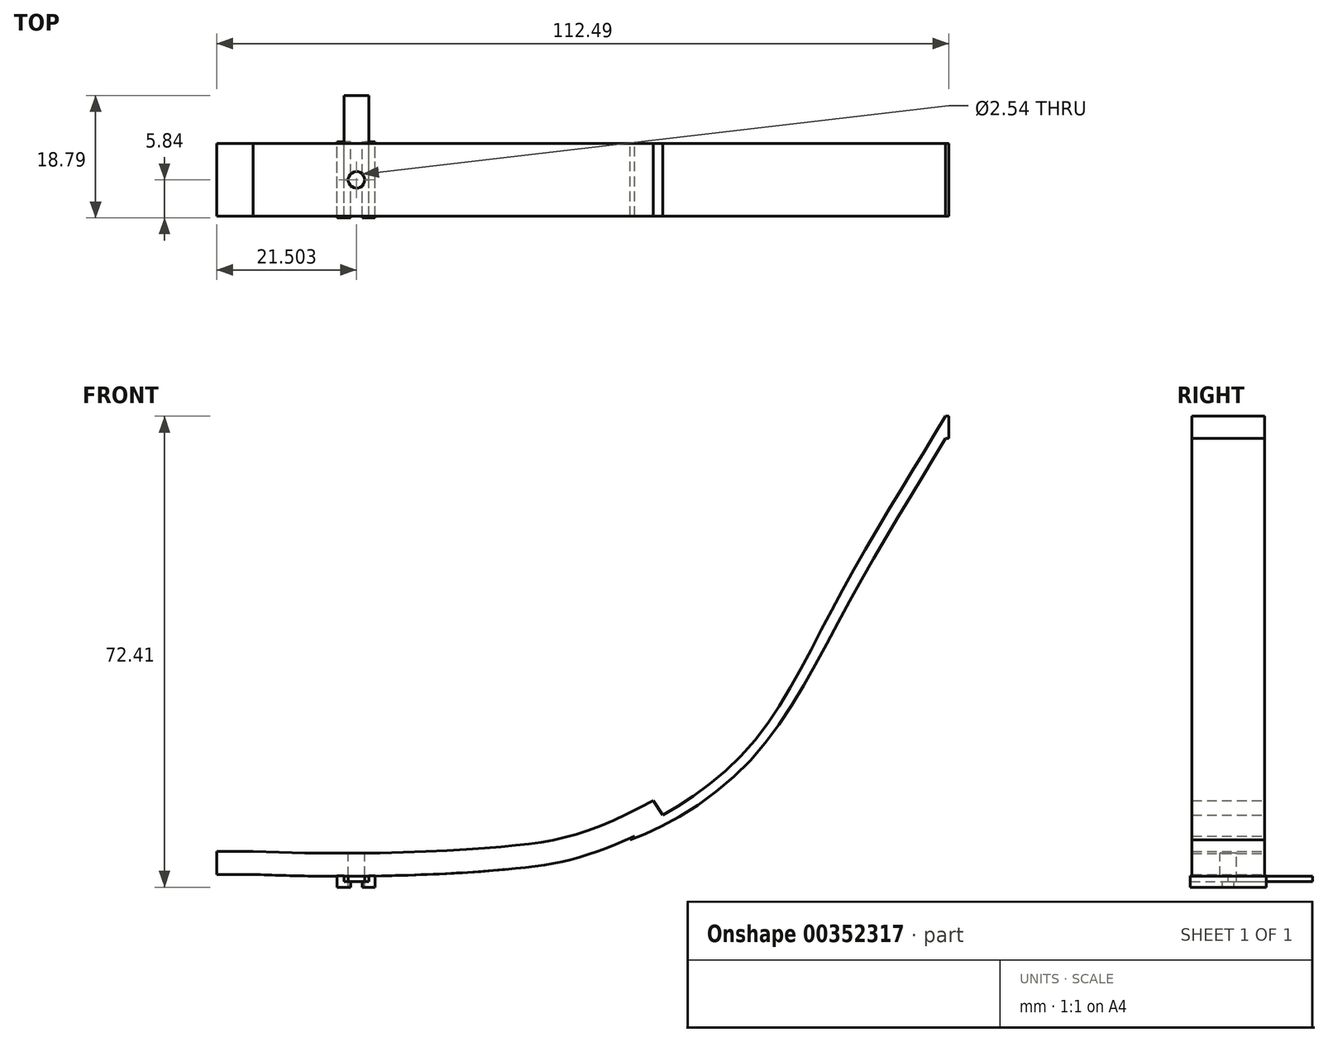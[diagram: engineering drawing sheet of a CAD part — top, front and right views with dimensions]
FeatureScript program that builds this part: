
annotation { "Feature Type Name" : "Feature", "Feature Type Description" : "" }
export const myFeature = defineFeature(function(context is Context, id is Id, definition is map)
    precondition{}
    {
        {
            var Q0;
            Q0=qCreatedBy(makeId("Front.planeOp"),FACE);
            var sketch = newSketch(context, id + "F0", { "sketchPlane" : qUnion([Q0])});
            skFitSpline(sketch, "E0", {"points": [v(-37, -20.34) * mm, v(0, -19.24) * mm, v(11.96, -16.65) * mm, v(24.57, -10.5) * mm], "startDerivative": vector(92.21, -3.16) * mm, "endDerivative": vector(48.05, 28.96) * mm});
            skSolve(sketch);
        }
        {
            var Q0;
            Q0=qCreatedBy(makeId("Front.planeOp"),FACE);
            var sketch = newSketch(context, id + "F1", { "sketchPlane" : qUnion([Q0])});
            skLineSegment(sketch, "E1.bottom", {"start": v(-45.97, -19.21) * mm, "end": v(-40.36, -19.21) * mm});
            skLineSegment(sketch, "E1.top", {"start": v(-45.97, -22.76) * mm, "end": v(-40.36, -22.76) * mm});
            skLineSegment(sketch, "E1.left", {"start": v(-45.97, -19.21) * mm, "end": v(-45.97, -22.76) * mm});
            skLineSegment(sketch, "E1.right", {"start": v(-40.36, -19.21) * mm, "end": v(-40.36, -22.76) * mm});
            skSolve(sketch);
        }
        {
            var Q0;
            Q0 = qSketchRegion(id + "F1", true);
            extrude(context, id + "F2", {"entities" : qUnion([Q0]), "depth" : 5.6 * mm, "hasSecondDirection" : true, "secondDirectionOppositeDirection" : true, "secondDirectionDepth" : 5.6 * mm});
        }
        {
            var Q0;
            Q0=makeQuery(id+"F2.opExtrude","SWEPT_FACE",FACE,{"disambiguationData":[OSD([sQuery(id+"F1.wireOp",EDGE,"E1.right")])]});
            var Q1;
            Q1=sQuery(id+"F0.wireOp",EDGE,"E0");
            sweep(context, id + "F3", {"operationType" : NewBodyOperationType.ADD, "profiles" : qUnion([Q0]), "path" : qUnion([Q1])});
        }
        {
            var Q0;
            Q0=qCreatedBy(makeId("Front.planeOp"),FACE);
            var sketch = newSketch(context, id + "F4", { "sketchPlane" : qUnion([Q0])});
            skFitSpline(sketch, "E2", {"points": [v(15.55, -18.84) * mm, v(35.24, -7.28) * mm, v(51.08, 16.97) * mm, v(65.62, 41.86) * mm], "startDerivative": vector(52.48, 11.3) * mm, "endDerivative": vector(39.11, 64.4) * mm});
            skSolve(sketch);
        }
        {
            var Q0;
            Q0=qCreatedBy(makeId("Front.planeOp"),FACE);
            var sketch = newSketch(context, id + "F5", { "sketchPlane" : qUnion([Q0])});
            skLineSegment(sketch, "E3.bottom", {"start": v(66.03, 47.68) * mm, "end": v(66.52, 47.68) * mm});
            skLineSegment(sketch, "E3.top", {"start": v(66.03, 44.28) * mm, "end": v(66.52, 44.28) * mm});
            skLineSegment(sketch, "E3.left", {"start": v(66.03, 47.68) * mm, "end": v(66.03, 44.28) * mm});
            skLineSegment(sketch, "E3.right", {"start": v(66.52, 47.68) * mm, "end": v(66.52, 44.28) * mm});
            skSolve(sketch);
        }
        {
            var Q0;
            Q0 = qSketchRegion(id + "F5", true);
            extrude(context, id + "F6", {"entities" : qUnion([Q0]), "depth" : 5.6 * mm, "hasSecondDirection" : true, "secondDirectionOppositeDirection" : true, "secondDirectionDepth" : 5.6 * mm});
        }
        {
            var Q0;
            Q0=makeQuery(id+"F6.opExtrude","SWEPT_FACE",FACE,{"disambiguationData":[OSD([sQuery(id+"F5.wireOp",EDGE,"E3.left")])]});
            var Q1;
            Q1=sQuery(id+"F4.wireOp",EDGE,"E2");
            sweep(context, id + "F7", {"operationType" : NewBodyOperationType.ADD, "profiles" : qUnion([Q0]), "path" : qUnion([Q1])});
        }
        {
            var Q0;
            Q0=qCreatedBy(makeId("Front.planeOp"),FACE);
            var sketch = newSketch(context, id + "F8", { "sketchPlane" : qUnion([Q0])});
            skLineSegment(sketch, "E4", {"start": v(-21.62, -23.07) * mm, "end": v(-21.62, -24.73) * mm});
            skLineSegment(sketch, "E5", {"start": v(-21.62, -24.73) * mm, "end": v(-23.56, -24.73) * mm});
            skLineSegment(sketch, "E6", {"start": v(-23.56, -24.73) * mm, "end": v(-23.56, -23.88) * mm});
            skLineSegment(sketch, "E7", {"start": v(-23.56, -23.88) * mm, "end": v(-22.6, -23.88) * mm});
            skPoint(sketch, "E7.endSnap0", {"position": v(-22.6, -24.73) * mm});
            skLineSegment(sketch, "E8", {"start": v(-22.6, -23.88) * mm, "end": v(-22.6, -23) * mm});
            skLineSegment(sketch, "E9", {"start": v(-22.6, -23) * mm, "end": v(-21.62, -23) * mm});
            skLineSegment(sketch, "E10", {"start": v(-21.62, -23) * mm, "end": v(-21.62, -23.07) * mm});
            skLineSegment(sketch, "E11", {"start": v(-25.37, -24.73) * mm, "end": v(-25.37, -23.88) * mm});
            skLineSegment(sketch, "E12", {"start": v(-25.37, -24.73) * mm, "end": v(-27.46, -24.73) * mm});
            skLineSegment(sketch, "E13", {"start": v(-25.37, -23.88) * mm, "end": v(-26.4, -23.88) * mm});
            skLineSegment(sketch, "E14", {"start": v(-26.4, -23.88) * mm, "end": v(-26.4, -23) * mm});
            skLineSegment(sketch, "E15", {"start": v(-27.46, -24.73) * mm, "end": v(-27.46, -23.88) * mm});
            skLineSegment(sketch, "E16", {"start": v(-27.46, -23.88) * mm, "end": v(-27.46, -23) * mm});
            skLineSegment(sketch, "E17", {"start": v(-27.46, -23) * mm, "end": v(-26.4, -23) * mm});
            skSolve(sketch);
        }
        {
            var Q0;
            Q0 = qSketchRegion(id + "F8", true);
            extrude(context, id + "F9", {"entities" : qUnion([Q0]), "operationType" : NewBodyOperationType.ADD, "depth" : 5.84 * mm, "hasSecondDirection" : true, "secondDirectionOppositeDirection" : true, "secondDirectionDepth" : 5.84 * mm});
        }
        {
            var Q0;
            Q0=qCreatedBy(makeId("Front.planeOp"),FACE);
            var sketch = newSketch(context, id + "F10", { "sketchPlane" : qUnion([Q0])});
            skLineSegment(sketch, "E18.bottom", {"start": v(-22.59, -23.02) * mm, "end": v(-26.4, -23.02) * mm});
            skLineSegment(sketch, "E18.top", {"start": v(-22.59, -23.87) * mm, "end": v(-26.4, -23.87) * mm});
            skLineSegment(sketch, "E18.left", {"start": v(-22.59, -23.02) * mm, "end": v(-22.59, -23.87) * mm});
            skLineSegment(sketch, "E18.right", {"start": v(-26.4, -23.02) * mm, "end": v(-26.4, -23.87) * mm});
            skSolve(sketch);
        }
        {
            var Q0;
            Q0 = qSketchRegion(id + "F10", true);
            extrude(context, id + "F11", {"entities" : qUnion([Q0]), "operationType" : NewBodyOperationType.ADD, "oppositeDirection" : true, "depth" : 12.95 * mm});
        }
        {
            var Q0;
            Q0=qCreatedBy(makeId("Top.planeOp"),FACE);
            var sketch = newSketch(context, id + "F12", { "sketchPlane" : qUnion([Q0])});
            skPoint(sketch, "E19", {"position": v(-24.47, 0) * mm});
            skSolve(sketch);
        }
        {
            var Q0;
            Q0=sQuery(id+"F12.wireOp",VERTEX,"E19");
            var Q1;
            Q1=makeQuery(id+"F2.opExtrude","SWEPT_BODY",BODY,{"disambiguationData":[OSD([sQuery(id+"F1.wireOp",EDGE,"E1.bottom"),sQuery(id+"F1.wireOp",EDGE,"E1.top"),sQuery(id+"F1.wireOp",EDGE,"E1.left"),sQuery(id+"F1.wireOp",EDGE,"E1.right")])]});
            hole(context, id + "F13", {"style" : HoleStyle.SIMPLE, "endStyle" : HoleEndStyle.THROUGH, "holeDiameter" : 2.54 * mm, "isTappedThrough" : true, "tappedDepth" : 12.7 * mm, "tapClearance" : 3, "locations" : qUnion([Q0]), "scope" : qUnion([Q1])});
        }
    });
